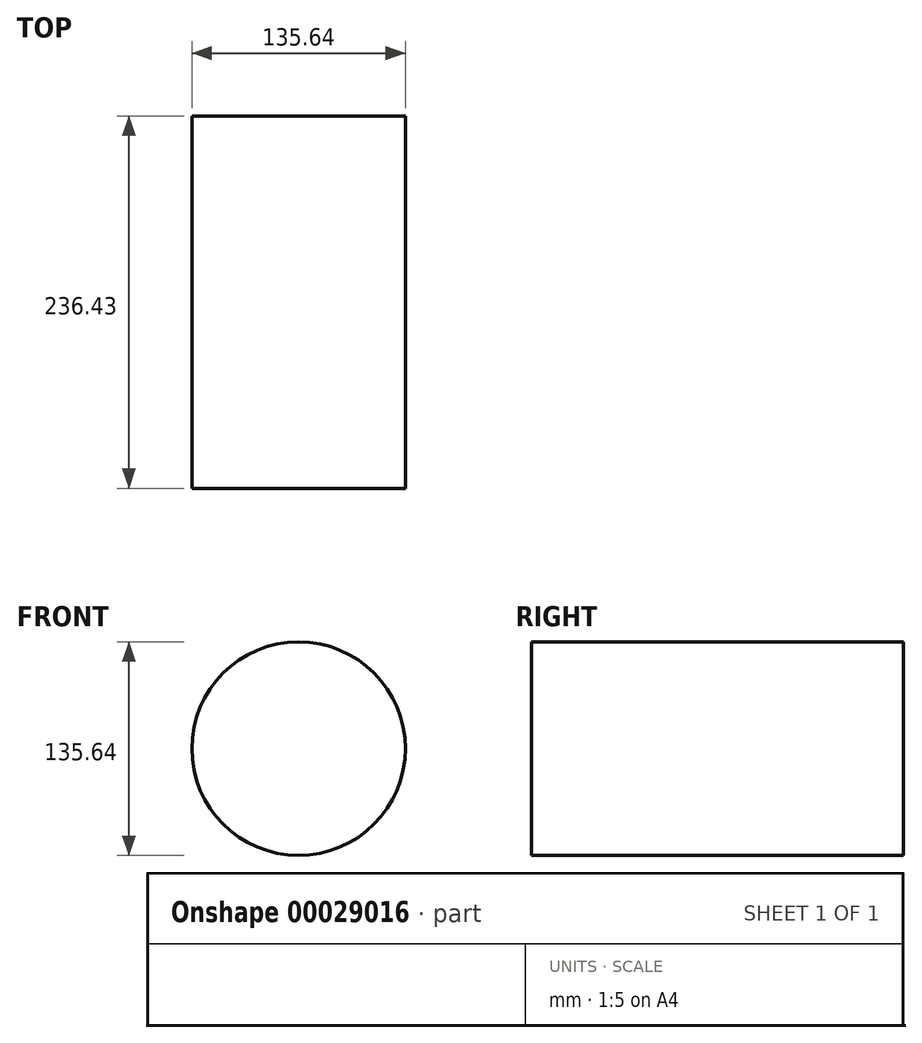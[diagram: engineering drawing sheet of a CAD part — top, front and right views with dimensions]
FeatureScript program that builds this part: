
annotation { "Feature Type Name" : "Feature", "Feature Type Description" : "" }
export const myFeature = defineFeature(function(context is Context, id is Id, definition is map)
    precondition{}
    {
        {
            var Q0;
            Q0=qCreatedBy(makeId("Front.planeOp"),FACE);
            var sketch = newSketch(context, id + "F1", { "sketchPlane" : qUnion([Q0])});
            skCircle(sketch, "E0", {"center": v(0, 0) * mm, "radius": 67.82 * mm});
            skSolve(sketch);
        }
        {
            var Q0;
            Q0=makeQuery(id+"F1.imprint","IMPRINT",FACE,{"disambiguationData":[TD([[makeQuery(id+"F1.imprint","IMPRINT",EDGE,{"derivedFrom":sQuery(id+"F1.wireOp",EDGE,"E0")}),1.0]])]});
            extrude(context, id + "F0", {"entities" : qUnion([Q0]), "oppositeDirection" : true, "depth" : 236.43 * mm});
        }
    });
